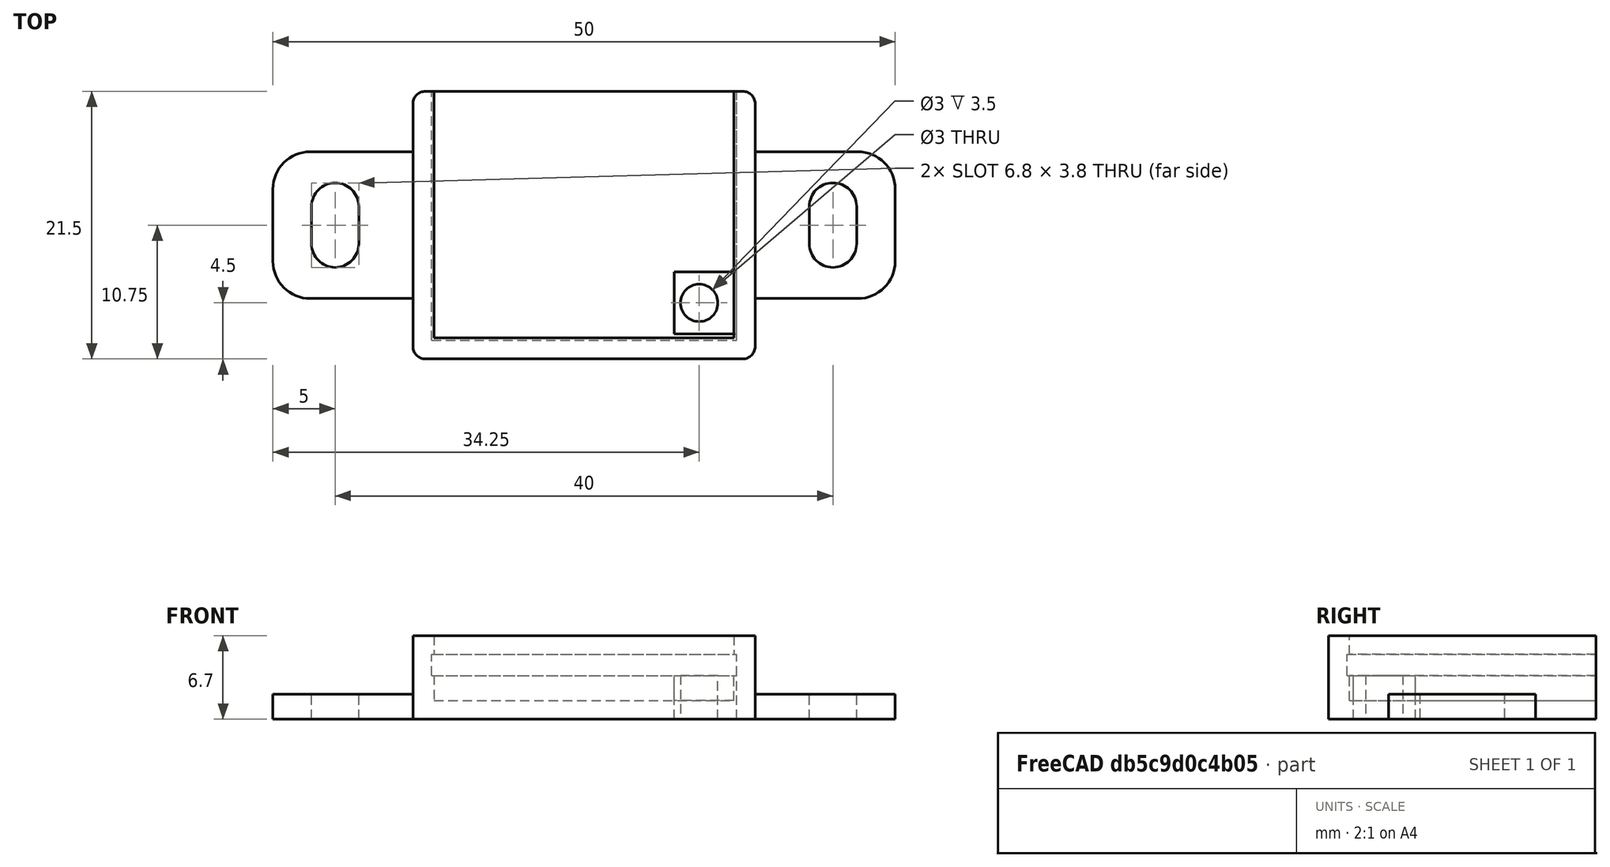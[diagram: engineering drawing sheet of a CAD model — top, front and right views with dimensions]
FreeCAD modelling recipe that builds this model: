
FCSTD DOCUMENT  (FreeCAD 0.21R33771 (Git))
Label: ens160+ant2x
License: FreeArt
LicenseURL: http://artlibre.org/licence/lal
objects: Part::Box×4, Part::MultiFuse×3, Part::Cut×3, Spreadsheet::Sheet×1, Part::Fillet×1, Part::Cylinder×1, Part::Feature×1, App::Part×1
note: 13 computed .brp shape members not serialized (recipe doc carries the construction recipe); baked Part::Feature solids carry a one-line shape summary decoded from their .brp

FEATURE [Spreadsheet::Sheet] Spreadsheet  label="p"
  cells = A1='pcb_x; B1(pcb_x)==24.5 mm; A2='pcb_y; B2(pcb_y)==20 mm; A3='pcb_z; B3(pcb_z)==1.7 mm; A4='pcb_under; B4(pcb_under)==2 mm; A5='side_wall; B5(side_wall)==1.5 mm; A6='pcb_side_lane; B6(pcb_side_lane)==0.2 mm; A7='bottom_wall; B7(bottom_wall)==1.5 mm; A8='pcb_above; B8(pcb_above)==1.5 mm; A9='hole_dist_x; B9(hole_dist_x)==23.5 mm; A10='hole_r; B10(hole_r)==1.5 mm; A11='hole_off_x; B11(hole_off_x)==21.5 mm; A12='hole_off_y; B12(hole_off_y)==3 mm; A13='hole_stand_size; B13(hole_stand_size)==5 mm
FEATURE [Part::Box] Box  label="external cube"
  AttacherType = Attacher::AttachEngine3D
  Height = 6.7
  Length = 27.5
  Width = 21.5
  expr: Height = <<p>>.bottom_wall + <<p>>.pcb_under + <<p>>.pcb_z + <<p>>.pcb_above
  expr: Length = <<p>>.pcb_x + 2 * <<p>>.side_wall
  expr: Width = <<p>>.pcb_y + <<p>>.side_wall
FEATURE [Part::Box] Box006  label="internal cube"
  AttacherType = Attacher::AttachEngine3D
  Height = 5.2
  Length = 24.1
  Placement = pos=(1.7,1.7,1.5) rot=(0,0,1;0rad)
  Width = 21.1
  expr: .Placement.Base.x = <<p>>.side_wall + <<p>>.pcb_side_lane
  expr: .Placement.Base.y = <<p>>.side_wall + <<p>>.pcb_side_lane
  expr: .Placement.Base.z = <<p>>.bottom_wall
  expr: Height = <<p>>.pcb_under + <<p>>.pcb_z + <<p>>.pcb_above
  expr: Length = <<p>>.pcb_x - 2 * <<p>>.pcb_side_lane
  expr: Width = <<p>>.pcb_y - 2 * <<p>>.pcb_side_lane + <<p>>.side_wall
FEATURE [Part::Box] Box007  label="pcb extract cube"
  AttacherType = Attacher::AttachEngine3D
  Height = 1.7
  Length = 24.5
  Placement = pos=(1.5,1.5,3.5) rot=(0,0,1;0rad)
  Width = 20
  expr: .Placement.Base.x = <<p>>.side_wall
  expr: .Placement.Base.y = <<p>>.side_wall
  expr: .Placement.Base.z = <<p>>.bottom_wall + <<p>>.pcb_under
  expr: Height = <<p>>.pcb_z
  expr: Length = <<p>>.pcb_x
  expr: Width = <<p>>.pcb_y
FEATURE [Part::MultiFuse] Fusion  label="extract fusion"
  Shapes = -> [Box006,Box007]
FEATURE [Part::Fillet] Fillet  label="external fillet"
  Base = -> Box
  Edges = 4 edges r=1: [Edge1,Edge3,Edge5,Edge7]
FEATURE [Part::Cylinder] Cylinder  label="hole"
  Angle = 360
  AttacherType = Attacher::AttachEngine3D
  FirstAngle = 0
  Height = 10
  Placement = pos=(23,4.5,0) rot=(0,0,1;0rad)
  Radius = 1.5
  SecondAngle = 0
  expr: .Placement.Base.x = <<p>>.side_wall + <<p>>.hole_off_x
  expr: .Placement.Base.y = <<p>>.hole_off_y + <<p>>.side_wall
  expr: Radius = <<p>>.hole_r
FEATURE [Part::Box] Box008  label="stand"
  AttacherType = Attacher::AttachEngine3D
  Height = 3.5
  Length = 5
  Placement = pos=(21,2,0) rot=(0,0,1;0rad)
  Width = 5
  expr: .Placement.Base.x = <<p>>.side_wall + <<p>>.hole_off_x - <<p>>.hole_stand_size / 2 + 0.5 mm
  expr: .Placement.Base.y = <<p>>.hole_off_y + <<p>>.side_wall - <<p>>.hole_stand_size / 2
  expr: Height = <<p>>.pcb_under + <<p>>.bottom_wall
  expr: Length = <<p>>.hole_stand_size
  expr: Width = <<p>>.hole_stand_size
FEATURE [Part::Cut] Cut003002  label="stand hole cut"
  Base = -> Box008
  Tool = -> Cylinder
FEATURE [Part::Feature] Cut004  label="attach plane x dir001"
  Placement = pos=(-11.25,4.85,0) rot=(0,0,1;0rad)
  shape: bbox 50 x 11.8 x 2 mm, 18 faces (baked)
FEATURE [Part::MultiFuse] Fusion001  label="body fusion"
  Shapes = -> [Fillet,Cut004]
FEATURE [Part::Cut] Cut  label="body cut003"
  Base = -> Fusion001
  Tool = -> Fusion
FEATURE [Part::MultiFuse] Fusion002  label="body fusion003"
  Shapes = -> [Cut,Box008]
FEATURE [Part::Cut] Cut003003  label="body cut"
  Base = -> Fusion002
  Tool = -> Cylinder
FEATURE [App::Part] Part  label="box part"
  Group = -> [Box,Fillet,Fusion001,Fusion,Box007,Box006,Cut,Cylinder,Box008,Cut003002,Fusion002,Cut003003]
  Origin = -> Origin
